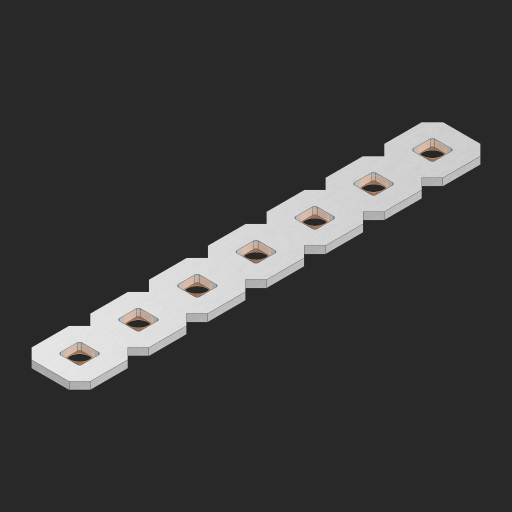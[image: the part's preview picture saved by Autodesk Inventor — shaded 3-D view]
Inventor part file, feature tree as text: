
AUTODESK INVENTOR PART (.ipt)
format: ipt  version: 2023 (Build 270158000, 158)  size: 341,504 bytes
history: native  units: in
note: dims shown in document units (in); Inventor stores cm internally (conversion verified against a paired STEP export)
features: other x8, extrude x6, sketch x2, pattern_linear x1
ambient origin geometry x8: Origin, YZ Plane, XZ Plane, XY Plane, X Axis, Y Axis, Z Axis, Center Point
bodies: Solid1 (feature_tree), Body (feature_tree)
feature tree (17):
  pattern_linear  "Rectangular Pattern1"  Spacing1=0.09in  [1 undecoded]
  sketch  "Sketch1"  dims[d1=0.5in]
  sketch  "Sketch2"  dims[d2=0.182in d3=0.09in d4=0.09in d5=0.09in d6=0.09in d7=0.09in d8=0.09in d9=0.09in d10=0.09in d11=0.02in d13=0.0in d14=0.172in d15=0.0625in d16=0.0in d19=0.5in d22=0.5in]
  other  "Srf1"
  other  "Srf126"
  other  "Srf127"
  other  "Srf128"
  other  "Srf129"
  other  "Srf130"
  other  "Srf131"
  other  "Circle"
  extrude  "ExtrusionSrf126"  Depth=0.09in
  extrude  "ExtrusionSrf127"  Depth=0.09in
  extrude  "ExtrusionSrf128"  Depth=0.09in
  extrude  "ExtrusionSrf129"  Depth=0.09in
  extrude  "ExtrusionSrf130"  Depth=0.09in
  extrude  "ExtrusionSrf131"  Depth=0.09in
note: 1 required parameter value undecoded (feature->parameter linkage not recoverable at this tier; creation-order binding heuristic only, values carry confidence <= 0.55)
